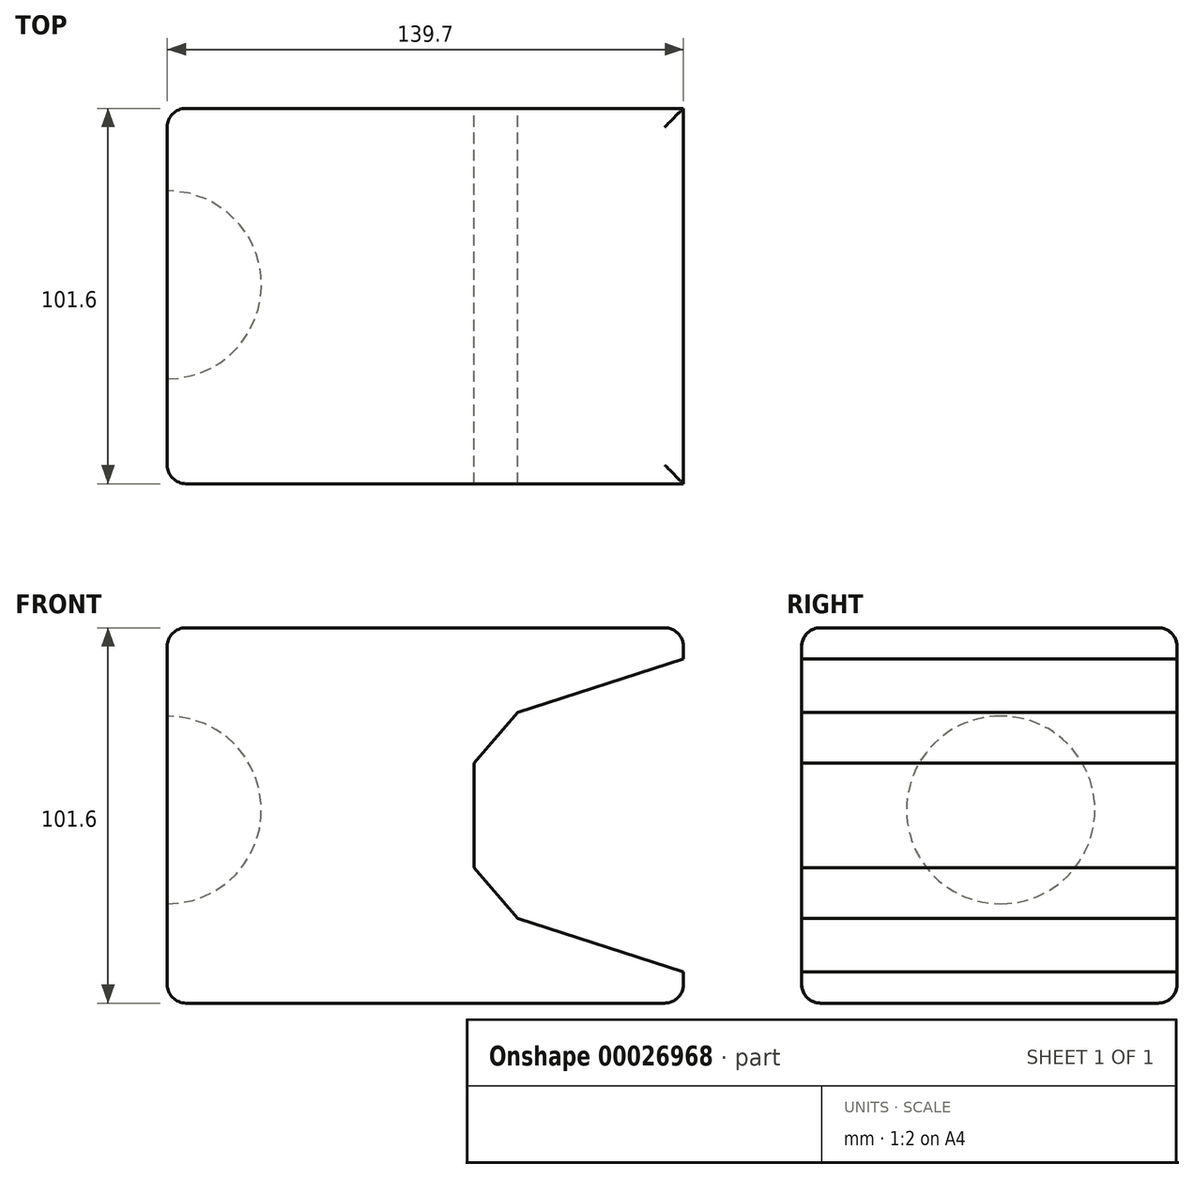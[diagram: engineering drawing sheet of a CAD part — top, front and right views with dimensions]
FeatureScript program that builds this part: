
annotation { "Feature Type Name" : "Feature", "Feature Type Description" : "" }
export const myFeature = defineFeature(function(context is Context, id is Id, definition is map)
    precondition{}
    {
        {
            var Q0;
            Q0=qCreatedBy(makeId("Front.planeOp"),FACE);
            var sketch = newSketch(context, id + "F0", { "sketchPlane" : qUnion([Q0])});
            skLineSegment(sketch, "E0.bottom", {"start": v(-84.07, 45.41) * mm, "end": v(55.63, 45.41) * mm});
            skLineSegment(sketch, "E0.top", {"start": v(-84.07, -56.19) * mm, "end": v(55.63, -56.19) * mm});
            skLineSegment(sketch, "E0.left", {"start": v(-84.07, 45.41) * mm, "end": v(-84.07, -56.19) * mm});
            skLineSegment(sketch, "E0.right", {"start": v(55.63, 45.41) * mm, "end": v(55.63, 36.93) * mm});
            skLineSegment(sketch, "E1", {"start": v(55.63, 36.93) * mm, "end": v(10.77, 22.47) * mm});
            skLineSegment(sketch, "E2", {"start": v(10.77, 22.47) * mm, "end": v(-1.05, 8.8) * mm});
            skLineSegment(sketch, "E3", {"start": v(-1.05, 8.8) * mm, "end": v(-1.05, -5.39) * mm});
            skLineSegment(sketch, "E4.MirrorCS", {"start": v(55.63, -47.7) * mm, "end": v(10.77, -33.25) * mm});
            skLineSegment(sketch, "E5.trimOffspring", {"start": v(55.63, -47.7) * mm, "end": v(55.63, -56.19) * mm});
            skLineSegment(sketch, "E6.MirrorCS", {"start": v(-1.05, -19.58) * mm, "end": v(-1.05, -5.39) * mm});
            skLineSegment(sketch, "E7.MirrorCS", {"start": v(10.77, -33.25) * mm, "end": v(-1.05, -19.58) * mm});
            skSolve(sketch);
        }
        {
            var Q0;
            Q0=makeQuery(id+"F0.imprint","IMPRINT",FACE,{"disambiguationData":[TD([[makeQuery(id+"F0.imprint","IMPRINT",EDGE,{"derivedFrom":sQuery(id+"F0.wireOp",EDGE,"E0.bottom")}),-1.0]])]});
            extrude(context, id + "F1", {"entities" : qUnion([Q0]), "depth" : 101.6 * mm});
        }
        {
            var Q0;
            Q0=makeQuery(id+"F1.opExtrude","SWEPT_FACE",FACE,{"disambiguationData":[OSD([sQuery(id+"F0.wireOp",EDGE,"E0.left")])]});
            var sketch = newSketch(context, id + "F2", { "sketchPlane" : qUnion([Q0])});
            skLineSegment(sketch, "E8", {"start": v(47.72, 21.5) * mm, "end": v(47.72, -29.3) * mm});
            skArc(sketch, "E9", {"start": v(47.72, -29.3) * mm, "mid": v(73.2, -3.9) * mm, "end": v(47.72, 21.5) * mm});
            skSolve(sketch);
        }
        {
            var Q0;
            Q0=makeQuery(id+"F2.imprint","IMPRINT",FACE,{"disambiguationData":[TD([[makeQuery(id+"F2.imprint","IMPRINT",EDGE,{"derivedFrom":sQuery(id+"F2.wireOp",EDGE,"E8")}),1.0]])]});
            var Q1;
            Q1=sQuery(id+"F2.wireOp",EDGE,"E8");
            revolve(context, id + "F3", {"operationType" : NewBodyOperationType.REMOVE, "entities" : qUnion([Q0]), "axis" : qUnion([Q1]), "revolveType" : RevolveType.FULL, "oppositeDirection" : true});
        }
        {
            var Q0;
            Q0=makeQuery(id+"F1.opExtrude","CAP_EDGE",EDGE,{"disambiguationData":[OSD([sQuery(id+"F0.wireOp",EDGE,"E0.left")])],"isStart":true});
            var Q1;
            Q1=makeQuery(id+"F1.opExtrude","CAP_EDGE",EDGE,{"disambiguationData":[OSD([sQuery(id+"F0.wireOp",EDGE,"E0.bottom")])],"isStart":true});
            var Q2;
            Q2=makeQuery(id+"F1.opExtrude","SWEPT_FACE",FACE,{"disambiguationData":[OSD([sQuery(id+"F0.wireOp",EDGE,"E0.bottom")])]});
            var Q3;
            Q3=makeQuery(id+"F1.opExtrude","CAP_EDGE",EDGE,{"disambiguationData":[OSD([sQuery(id+"F0.wireOp",EDGE,"E0.top")])],"isStart":false});
            var Q4;
            Q4=makeQuery(id+"F1.opExtrude","SWEPT_EDGE",EDGE,{"disambiguationData":[OSD([sQuery(id+"F0.wireOp",EDGE,"E0.top"),sQuery(id+"F0.wireOp",EDGE,"E0.left")])]});
            var Q5;
            Q5=makeQuery(id+"F1.opExtrude","CAP_EDGE",EDGE,{"disambiguationData":[OSD([sQuery(id+"F0.wireOp",EDGE,"E0.top")])],"isStart":true});
            var Q6;
            Q6=makeQuery(id+"F1.opExtrude","CAP_EDGE",EDGE,{"disambiguationData":[OSD([sQuery(id+"F0.wireOp",EDGE,"E0.left")])],"isStart":false});
            var Q7;
            Q7=makeQuery(id+"F1.opExtrude","SWEPT_EDGE",EDGE,{"disambiguationData":[OSD([sQuery(id+"F0.wireOp",EDGE,"E0.top"),sQuery(id+"F0.wireOp",EDGE,"E5.trimOffspring")])]});
            fillet(context, id + "F4", {"entities" : qUnion([Q0, Q1, Q2, Q3, Q4, Q5, Q6, Q7]), "radius" : 5.08 * mm, "tangentPropagation" : true, "allowEdgeOverflow" : false});
        }
    });
